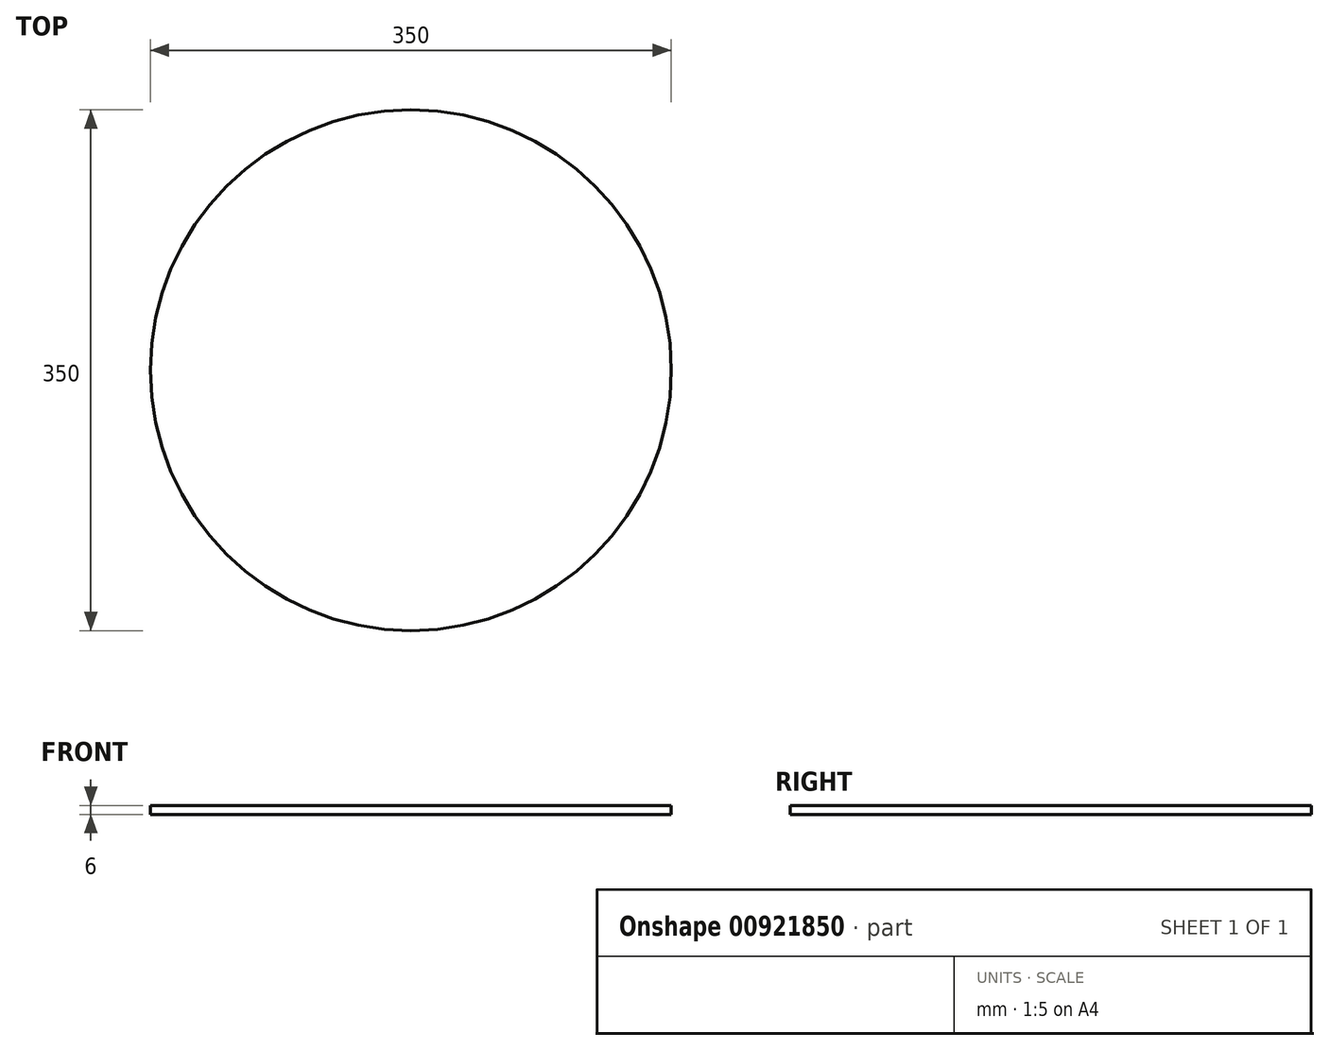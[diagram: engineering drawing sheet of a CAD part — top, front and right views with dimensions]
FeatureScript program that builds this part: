
annotation { "Feature Type Name" : "Feature", "Feature Type Description" : "" }
export const myFeature = defineFeature(function(context is Context, id is Id, definition is map)
    precondition{}
    {
        {
            var Q0;
            Q0=qCreatedBy(makeId("Top.planeOp"),FACE);
            var sketch = newSketch(context, id + "F0", { "sketchPlane" : qUnion([Q0])});
            skCircle(sketch, "E0", {"center": v(0, 0) * mm, "radius": 175 * mm});
            skSolve(sketch);
        }
        {
            var Q0;
            Q0=makeQuery(id+"F0.imprint","IMPRINT",FACE,{"disambiguationData":[TD([[makeQuery(id+"F0.imprint","IMPRINT",EDGE,{"derivedFrom":sQuery(id+"F0.wireOp",EDGE,"E0")}),1.0]])]});
            extrude(context, id + "F1", {"entities" : qUnion([Q0]), "oppositeDirection" : true, "depth" : 6 * mm, "offsetDistance" : 25 * mm});
        }
    });
